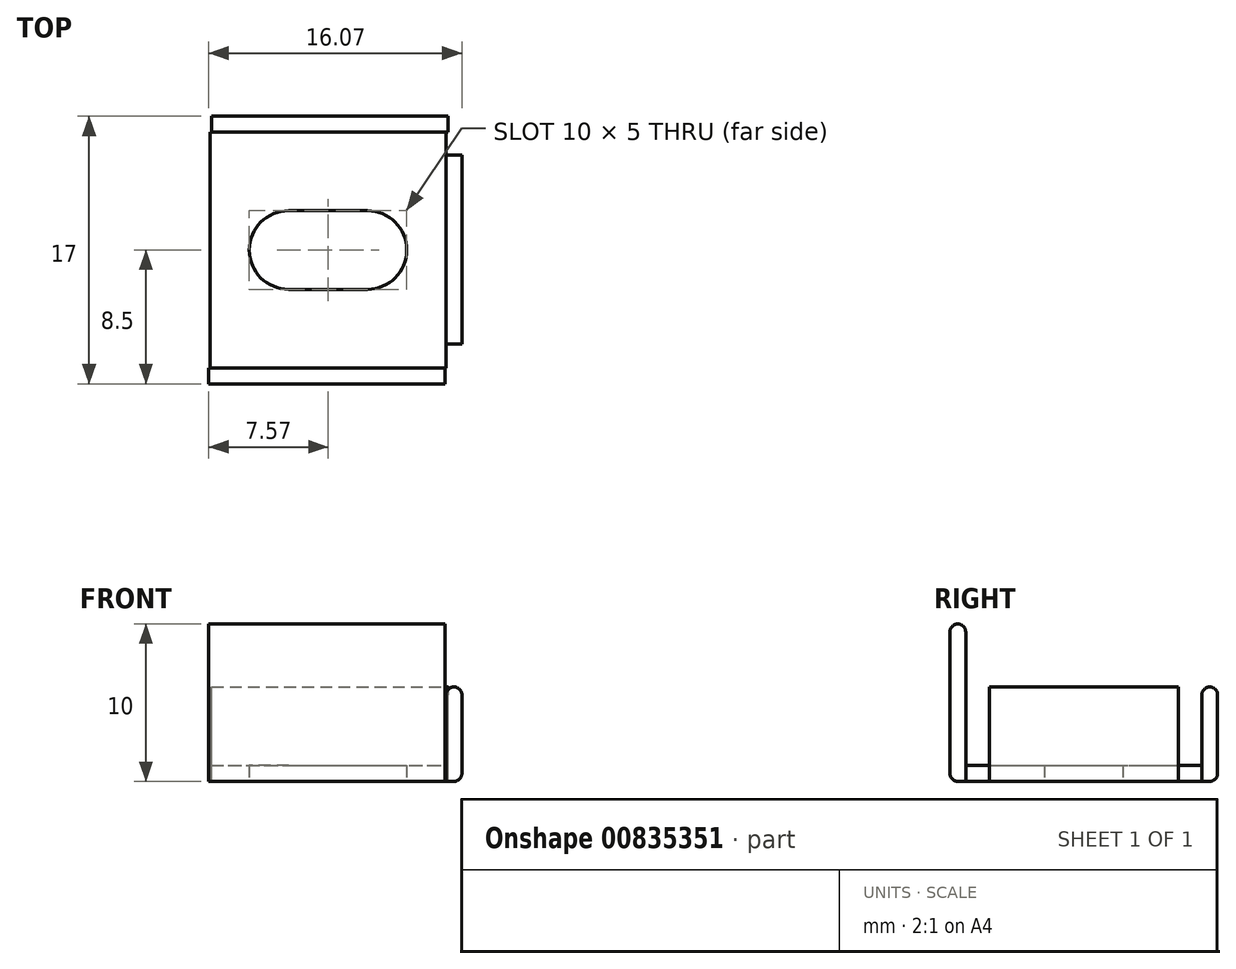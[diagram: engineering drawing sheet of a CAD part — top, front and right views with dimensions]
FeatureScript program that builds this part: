
annotation { "Feature Type Name" : "Feature", "Feature Type Description" : "" }
export const myFeature = defineFeature(function(context is Context, id is Id, definition is map)
    precondition{}
    {
        {
            var Q0;
            Q0=qCreatedBy(makeId("Top.planeOp"),FACE);
            var sketch = newSketch(context, id + "F0", { "sketchPlane" : qUnion([Q0])});
            skLineSegment(sketch, "E0.bottom", {"start": v(-7.5, -7.5) * mm, "end": v(7.5, -7.5) * mm});
            skLineSegment(sketch, "E0.top", {"start": v(-7.5, 7.5) * mm, "end": v(7.5, 7.5) * mm});
            skLineSegment(sketch, "E0.left", {"start": v(-7.5, -7.5) * mm, "end": v(-7.5, 7.5) * mm});
            skLineSegment(sketch, "E0.right", {"start": v(7.5, -7.5) * mm, "end": v(7.5, 7.5) * mm});
            skPoint(sketch, "E0.middle", {"position": v(0, 0) * mm});
            skLineSegment(sketch, "E1.bottom", {"start": v(-2.5, 2.5) * mm, "end": v(2.5, 2.5) * mm});
            skLineSegment(sketch, "E1.top", {"start": v(-2.5, -2.5) * mm, "end": v(2.5, -2.5) * mm});
            skLineSegment(sketch, "E1.left", {"start": v(-5, 0) * mm, "end": v(-5, 0) * mm});
            skLineSegment(sketch, "E1.right", {"start": v(5, 0) * mm, "end": v(5, 0) * mm});
            skPoint(sketch, "E2.visualSharp", {"position": v(5, 2.5) * mm});
            skArc(sketch, "E2.filletArc", {"start": v(5, 0) * mm, "mid": v(4.27, 1.77) * mm, "end": v(2.5, 2.5) * mm});
            skPoint(sketch, "E3.visualSharp", {"position": v(5, -2.5) * mm});
            skArc(sketch, "E3.filletArc", {"start": v(2.5, -2.5) * mm, "mid": v(4.27, -1.77) * mm, "end": v(5, 0) * mm});
            skPoint(sketch, "E4.visualSharp", {"position": v(-5, -2.5) * mm});
            skArc(sketch, "E4.filletArc", {"start": v(-5, 0) * mm, "mid": v(-4.27, -1.77) * mm, "end": v(-2.5, -2.5) * mm});
            skPoint(sketch, "E5.visualSharp", {"position": v(-5, 2.5) * mm});
            skArc(sketch, "E5.filletArc", {"start": v(-2.5, 2.5) * mm, "mid": v(-4.27, 1.77) * mm, "end": v(-5, 0) * mm});
            skSolve(sketch);
        }
        {
            var Q0;
            Q0=sQuery(id+"F0.wireOp",EDGE,"E0.bottom");
            cPoint(context, id + "F1", {"entities" : qUnion([Q0]), "parameter" : 0.5});
        }
        {
            var Q0;
            Q0=qCreatedBy(id+"F1",VERTEX);
            var Q1;
            Q1=qCreatedBy(makeId("Front.planeOp"),FACE);
            cPlane(context, id + "F2", {"entities" : qUnion([Q0, Q1]), "cplaneType" : CPlaneType.PLANE_POINT, "offset" : 25 * mm, "width" : 150 * mm, "height" : 150 * mm});
        }
        {
            var Q0;
            Q0=sQuery(id+"F0.wireOp",EDGE,"E0.top");
            cPoint(context, id + "F3", {"entities" : qUnion([Q0]), "parameter" : 0.5});
        }
        {
            var Q0;
            Q0=qCreatedBy(id+"F3",VERTEX);
            var Q1;
            Q1=qCreatedBy(id+"F2.planeOp",FACE);
            cPlane(context, id + "F4", {"entities" : qUnion([Q0, Q1]), "cplaneType" : CPlaneType.PLANE_POINT, "offset" : 25 * mm, "width" : 150 * mm, "height" : 150 * mm});
        }
        {
            var Q0;
            Q0=sQuery(id+"F0.wireOp",EDGE,"E0.right");
            cPoint(context, id + "F5", {"entities" : qUnion([Q0]), "parameter" : 0.5});
        }
        {
            var Q0;
            Q0=qCreatedBy(id+"F5",VERTEX);
            var Q1;
            Q1=qCreatedBy(makeId("Right.planeOp"),FACE);
            cPlane(context, id + "F6", {"entities" : qUnion([Q0, Q1]), "cplaneType" : CPlaneType.PLANE_POINT, "offset" : 25 * mm, "width" : 150 * mm, "height" : 150 * mm});
        }
        {
            var Q0;
            Q0=qCreatedBy(id+"F2.planeOp",FACE);
            var sketch = newSketch(context, id + "F7", { "sketchPlane" : qUnion([Q0])});
            skLineSegment(sketch, "E6.bottom", {"start": v(-7.57, 0) * mm, "end": v(7.43, 0) * mm});
            skLineSegment(sketch, "E6.top", {"start": v(-7.57, 10) * mm, "end": v(7.43, 10) * mm});
            skLineSegment(sketch, "E6.left", {"start": v(-7.57, 0) * mm, "end": v(-7.57, 10) * mm});
            skLineSegment(sketch, "E6.right", {"start": v(7.43, 0) * mm, "end": v(7.43, 10) * mm});
            skSolve(sketch);
        }
        {
            var Q0;
            Q0=qCreatedBy(id+"F4.planeOp",FACE);
            var sketch = newSketch(context, id + "F8", { "sketchPlane" : qUnion([Q0])});
            skLineSegment(sketch, "E7.bottom", {"start": v(7.61, 0) * mm, "end": v(-7.39, 0) * mm});
            skLineSegment(sketch, "E7.top", {"start": v(7.61, 6) * mm, "end": v(-7.39, 6) * mm});
            skLineSegment(sketch, "E7.left", {"start": v(7.61, 0) * mm, "end": v(7.61, 6) * mm});
            skLineSegment(sketch, "E7.right", {"start": v(-7.39, 0) * mm, "end": v(-7.39, 6) * mm});
            skSolve(sketch);
        }
        {
            var Q0;
            Q0=qCreatedBy(id+"F6.planeOp",FACE);
            var sketch = newSketch(context, id + "F9", { "sketchPlane" : qUnion([Q0])});
            skLineSegment(sketch, "E8.bottom", {"start": v(-5.98, 0) * mm, "end": v(6.02, 0) * mm});
            skLineSegment(sketch, "E8.top", {"start": v(-5.98, 6) * mm, "end": v(6.02, 6) * mm});
            skLineSegment(sketch, "E8.left", {"start": v(-5.98, 0) * mm, "end": v(-5.98, 6) * mm});
            skLineSegment(sketch, "E8.right", {"start": v(6.02, 0) * mm, "end": v(6.02, 6) * mm});
            skLineSegment(sketch, "E9", {"start": v(0.02, 6) * mm, "end": v(0.02, 0) * mm, "construction": true});
            skSolve(sketch);
        }
        {
            var Q0;
            Q0=qSketchRegion(id+"F9",true);
            extrude(context, id + "F10", {"entities" : qUnion([Q0]), "depth" : 1 * mm, "offsetDistance" : 25 * mm});
        }
        {
            var Q0;
            Q0=qSketchRegion(id+"F8",true);
            extrude(context, id + "F11", {"entities" : qUnion([Q0]), "operationType" : NewBodyOperationType.ADD, "oppositeDirection" : true, "depth" : 1 * mm, "offsetDistance" : 25 * mm});
        }
        {
            var Q0;
            Q0=makeQuery(id+"F7.imprint","IMPRINT",FACE,{"disambiguationData":[TD([[makeQuery(id+"F7.imprint","IMPRINT",EDGE,{"derivedFrom":sQuery(id+"F7.wireOp",EDGE,"E6.bottom")}),1.0]])]});
            extrude(context, id + "F12", {"entities" : qUnion([Q0]), "depth" : 1 * mm, "offsetDistance" : 25 * mm});
        }
        {
            var Q0;
            Q0=makeQuery(id+"F0.imprint","IMPRINT",FACE,{"disambiguationData":[TD([[makeQuery(id+"F0.imprint","IMPRINT",EDGE,{"derivedFrom":sQuery(id+"F0.wireOp",EDGE,"E0.bottom")}),1.0]])]});
            extrude(context, id + "F13", {"entities" : qUnion([Q0]), "operationType" : NewBodyOperationType.ADD, "depth" : 1 * mm, "offsetDistance" : 25 * mm});
        }
        {
            var Q0;
            Q0=makeQuery(id+"F10.opExtrude","CAP_EDGE",EDGE,{"disambiguationData":[OSD([sQuery(id+"F9.wireOp",EDGE,"E8.top")])],"isStart":false});
            fillet(context, id + "F14", {"entities" : qUnion([Q0]), "radius" : 0.5 * mm, "tangentPropagation" : true, "allowEdgeOverflow" : false});
        }
        {
            var Q0;
            Q0=makeQuery(id+"F10.opExtrude","CAP_EDGE",EDGE,{"disambiguationData":[OSD([sQuery(id+"F9.wireOp",EDGE,"E8.top")])],"isStart":true});
            var Q1;
            Q1=makeQuery(id+"F10.opExtrude","CAP_EDGE",EDGE,{"disambiguationData":[OSD([sQuery(id+"F9.wireOp",EDGE,"E8.bottom")])],"isStart":false});
            var Q2;
            Q2=makeQuery(id+"F12.opExtrude","CAP_EDGE",EDGE,{"disambiguationData":[OSD([sQuery(id+"F7.wireOp",EDGE,"E6.top")])],"isStart":false});
            var Q3;
            Q3=makeQuery(id+"F12.opExtrude","CAP_EDGE",EDGE,{"disambiguationData":[OSD([sQuery(id+"F7.wireOp",EDGE,"E6.top")])],"isStart":true});
            fillet(context, id + "F15", {"entities" : qUnion([Q0, Q1, Q2, Q3]), "radius" : 0.5 * mm, "tangentPropagation" : true, "allowEdgeOverflow" : false});
        }
        {
            var Q0;
            Q0=makeQuery(id+"F12.opExtrude","CAP_EDGE",EDGE,{"disambiguationData":[OSD([sQuery(id+"F7.wireOp",EDGE,"E6.bottom")])],"isStart":false});
            var Q1;
            Q1=makeQuery(id+"F11.opExtrude","CAP_EDGE",EDGE,{"disambiguationData":[OSD([sQuery(id+"F8.wireOp",EDGE,"E7.bottom")])],"isStart":false});
            var Q2;
            Q2=makeQuery(id+"F11.opExtrude","CAP_EDGE",EDGE,{"disambiguationData":[OSD([sQuery(id+"F8.wireOp",EDGE,"E7.top")])],"isStart":false});
            var Q3;
            Q3=makeQuery(id+"F11.opExtrude","CAP_EDGE",EDGE,{"disambiguationData":[OSD([sQuery(id+"F8.wireOp",EDGE,"E7.top")])],"isStart":true});
            fillet(context, id + "F16", {"entities" : qUnion([Q0, Q1, Q2, Q3]), "radius" : 0.5 * mm, "tangentPropagation" : true, "allowEdgeOverflow" : false});
        }
        {
            var Q0;
            Q0=makeQuery(id+"F0.imprint","IMPRINT",FACE,{"disambiguationData":[TD([[makeQuery(id+"F0.imprint","IMPRINT",EDGE,{"derivedFrom":sQuery(id+"F0.wireOp",EDGE,"E1.bottom")}),-1.0]])]});
            extrude(context, id + "F17", {"entities" : qUnion([Q0]), "operationType" : NewBodyOperationType.REMOVE, "depth" : 1 * mm, "offsetDistance" : 25 * mm});
        }
    });
